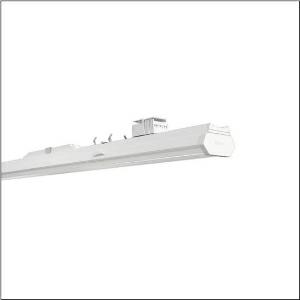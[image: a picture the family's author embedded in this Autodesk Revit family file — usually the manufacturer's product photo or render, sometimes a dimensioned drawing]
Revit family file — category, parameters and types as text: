
# Revit family: licross_11_protected_ho_51tp13cn4e5s
name_source: partatom
category: Lighting Fixtures
units: mm (PartAtom-declared; Revit-internal decimal feet)

## family parameters
Cut with Voids When Loaded = No
Host = Face
Light Source = No
Part Type = Normal
Room Calculation Point = No
Round Connector Dimension = Use Diameter
Shared = No

## types (1)
- --- (1 x LED, 14500 lm, 77.6 W, 4000K)
    Apparent Load = 78 VA
    CIE Flux Codes = 89 96 99 100 99
    Color Rendering = 80
    Color Temperature = 4000K
    Default Elevation = 1800 mm
    Description = Licross 11 Protected HO, luminaire insert, of sheet steel, galvanised, coil coated, white, length: 1.500mm, width: 90mm, height: 101mm, LED rated luminous flux: 14.500lm, light colour: 840, SDCM (Standard Deviation of Colour Matching)MacAdam ≤ 2 SDCM (initial), control gear: ON/OFF Multilumen, CLOi, with plug, 3-pole, with phase selection, mains connection: 220..240V, AC, 50/60Hz, start of lifetime: 78W, end of service life: 87W, internal wiring halogen-free, primary light control with lens, of plastic, primary optical cover: cover, of PMMA, light emission: direct distribution, primary light characteristic: symmetric, protection rating (complete): IP64, insulation class (complete): insulation class I (protective earthing), certification: CE, ENEC, VDE, UKCA, protection symbol: D if used in an environment with conductive dust loads with corresponding accessories, impact resistance: IK06, permissible ambient temperature for indoor applications: -35..+35°C, corresponds to IFS (International Featured Standards) requirements for safety and quality in the food industry, reducing of maximum allowable ambient temperature of 5°C with ceiling mounting, LABS conformity tested according to VDMA 24364:2018-05, The light source and the operating device comply with the requirements of the Ecodesign Regulation (EU) 2019/2020 and are replaceable in accordance with this regulation, packaging unit: 1 piece
    Height = 92 mm
    Lamp = 1 x LED
    Lamp Light Flux = 14500 lm
    Lamp Power = 77.6 W
    Lamp count = 1
    Length = 1500 mm
    Luminous efficacy = 187 lm/W
    Manufacturer = Siteco
    ModVariant = No
    Model = 51TP13CN4E5S
    Mounting Place = Ceiling
    Mounting Type = Pendant
    Number of Poles = 1
    OnlyDefault = Yes
    Power Factor = 1
    Product Name = Licross 11 Protected HO
    Product group = luminaire insert | ceiling pendant
    ProductGroupID = 901
    Protection Class = Protection class I
    Protection Degree = IP 64
    RLX_Detail_Level = 1
    RLX_Emergency_Light_Flux = 0 lm
    RLX_Emergency_Type = 0
    RLX_Emergency_Type_DB = No
    RlxData = <blob elided: 22389 chars, md5=efa269a9>
    Socket = socket
    Standby Power = 0 W
    System Light Flux = 14500 lm
    System Power = 78 W
    Type Comments = factory setting: luminous flux: 100 % | (A | C | E) | 181 mA
    Type Image = l_1256148.jpg
    URL = http://relux.com
    VarID = @adj_091021
    Voltage = 0 V
    Weight = 0.00 kg
    Width = 88 mm

## geometry (parser evidence)
native form markers: Blend x4, Sweep x12
no freeform markers — native parametric forms only
